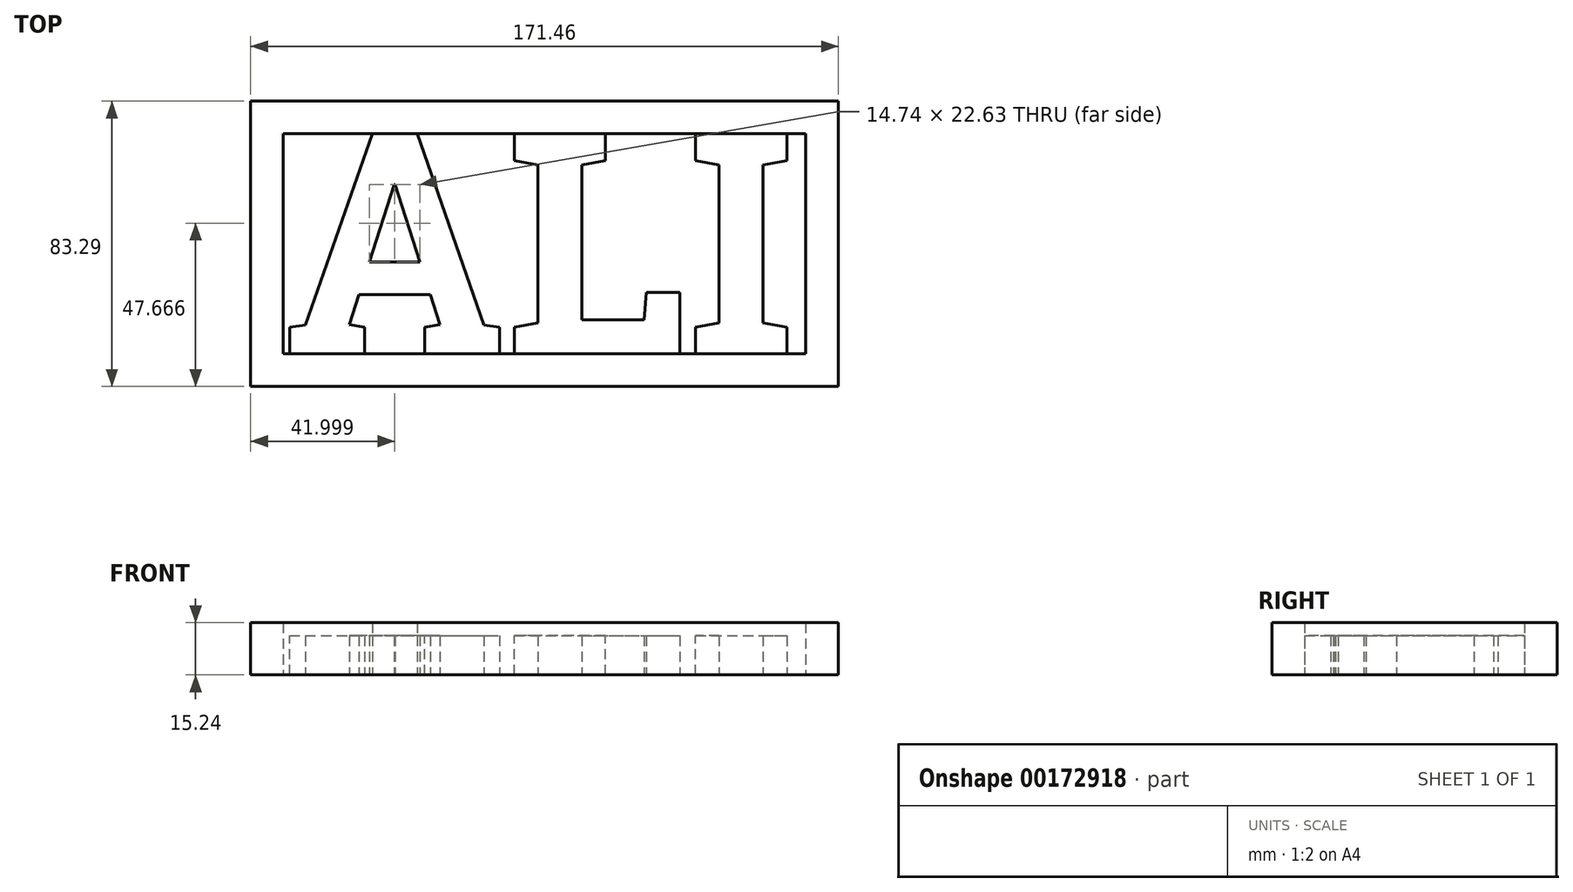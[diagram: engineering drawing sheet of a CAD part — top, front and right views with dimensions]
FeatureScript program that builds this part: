
annotation { "Feature Type Name" : "Feature", "Feature Type Description" : "" }
export const myFeature = defineFeature(function(context is Context, id is Id, definition is map)
    precondition{}
    {
        {
            var Q0;
            Q0=qCreatedBy(makeId("Top.planeOp"),FACE);
            var sketch = newSketch(context, id + "F0", { "sketchPlane" : qUnion([Q0])});
            skLineSegment(sketch, "E0.bottom", {"start": v(0, 0) * mm, "end": v(152.4, 0) * mm});
            skLineSegment(sketch, "E0.top", {"start": v(0, 9.53) * mm, "end": v(152.4, 9.53) * mm});
            skLineSegment(sketch, "E0.left", {"start": v(0, 0) * mm, "end": v(0, 9.53) * mm});
            skLineSegment(sketch, "E0.right", {"start": v(152.4, 0) * mm, "end": v(152.4, 9.53) * mm});
            skText(sketch, "E1", { "text": "ALI", "fontName": "RobotoSlab-Bold.ttf"});
            const initialGuessF0  = {"E1": [0, 0.00953, 1, 0, 0.06505]};
            skSetInitialGuess(sketch, initialGuessF0);
            skSolve(sketch);
        }
        {
            var Q0;
            Q0=qSketchRegion(id+"F0",true);
            extrude(context, id + "F1", {"entities" : qUnion([Q0]), "depth" : 11.43 * mm});
        }
        {
            var Q0;
            Q0=makeQuery(id+"F1.opExtrude","CAP_FACE",FACE,{"disambiguationData":[OSD([sQuery(id+"F0.wireOp",EDGE,"E0.bottom"),sQuery(id+"F0.wireOp",EDGE,"E0.top"),sQuery(id+"F0.wireOp",EDGE,"E0.left"),sQuery(id+"F0.wireOp",EDGE,"E0.right"),sQuery(id+"F0.wireOp",EDGE,"E1.sketch_text.stroke-0"),sQuery(id+"F0.wireOp",EDGE,"E1.sketch_text.stroke-1"),sQuery(id+"F0.wireOp",EDGE,"E1.sketch_text.stroke-2"),sQuery(id+"F0.wireOp",EDGE,"E1.sketch_text.stroke-3"),sQuery(id+"F0.wireOp",EDGE,"E1.sketch_text.stroke-4"),sQuery(id+"F0.wireOp",EDGE,"E1.sketch_text.stroke-5"),sQuery(id+"F0.wireOp",EDGE,"E1.sketch_text.stroke-6"),sQuery(id+"F0.wireOp",EDGE,"E1.sketch_text.stroke-7"),sQuery(id+"F0.wireOp",EDGE,"E1.sketch_text.stroke-8"),sQuery(id+"F0.wireOp",EDGE,"E1.sketch_text.stroke-9"),sQuery(id+"F0.wireOp",EDGE,"E1.sketch_text.stroke-10"),sQuery(id+"F0.wireOp",EDGE,"E1.sketch_text.stroke-11"),sQuery(id+"F0.wireOp",EDGE,"E1.sketch_text.stroke-12"),sQuery(id+"F0.wireOp",EDGE,"E1.sketch_text.stroke-13"),sQuery(id+"F0.wireOp",EDGE,"E1.sketch_text.stroke-14"),sQuery(id+"F0.wireOp",EDGE,"E1.sketch_text.stroke-15"),sQuery(id+"F0.wireOp",EDGE,"E1.sketch_text.stroke-16"),sQuery(id+"F0.wireOp",EDGE,"E1.sketch_text.stroke-17"),sQuery(id+"F0.wireOp",EDGE,"E1.sketch_text.stroke-18"),sQuery(id+"F0.wireOp",EDGE,"E1.sketch_text.stroke-19"),sQuery(id+"F0.wireOp",EDGE,"E1.sketch_text.stroke-20"),sQuery(id+"F0.wireOp",EDGE,"E1.sketch_text.stroke-21"),sQuery(id+"F0.wireOp",EDGE,"E1.sketch_text.stroke-22"),sQuery(id+"F0.wireOp",EDGE,"E1.sketch_text.stroke-23"),sQuery(id+"F0.wireOp",EDGE,"E1.sketch_text.stroke-24"),sQuery(id+"F0.wireOp",EDGE,"E1.sketch_text.stroke-25"),sQuery(id+"F0.wireOp",EDGE,"E1.sketch_text.stroke-26"),sQuery(id+"F0.wireOp",EDGE,"E1.sketch_text.stroke-27"),sQuery(id+"F0.wireOp",EDGE,"E1.sketch_text.stroke-28"),sQuery(id+"F0.wireOp",EDGE,"E1.sketch_text.stroke-29"),sQuery(id+"F0.wireOp",EDGE,"E1.sketch_text.stroke-30"),sQuery(id+"F0.wireOp",EDGE,"E1.sketch_text.stroke-31"),sQuery(id+"F0.wireOp",EDGE,"E1.sketch_text.stroke-32"),sQuery(id+"F0.wireOp",EDGE,"E1.sketch_text.stroke-33"),sQuery(id+"F0.wireOp",EDGE,"E1.sketch_text.stroke-34"),sQuery(id+"F0.wireOp",EDGE,"E1.sketch_text.stroke-35"),sQuery(id+"F0.wireOp",EDGE,"E1.sketch_text.stroke-36"),sQuery(id+"F0.wireOp",EDGE,"E1.sketch_text.stroke-37"),sQuery(id+"F0.wireOp",EDGE,"E1.sketch_text.stroke-38"),sQuery(id+"F0.wireOp",EDGE,"E1.sketch_text.stroke-39"),sQuery(id+"F0.wireOp",EDGE,"E1.sketch_text.stroke-40"),sQuery(id+"F0.wireOp",EDGE,"E1.sketch_text.stroke-42"),sQuery(id+"F0.wireOp",EDGE,"E1.sketch_text.stroke-43"),sQuery(id+"F0.wireOp",EDGE,"E1.sketch_text.stroke-44"),sQuery(id+"F0.wireOp",EDGE,"E1.sketch_text.stroke-45"),sQuery(id+"F0.wireOp",EDGE,"E1.sketch_text.stroke-46"),sQuery(id+"F0.wireOp",EDGE,"E1.sketch_text.stroke-47"),sQuery(id+"F0.wireOp",EDGE,"E1.sketch_text.stroke-48"),sQuery(id+"F0.wireOp",EDGE,"E1.sketch_text.stroke-50"),sQuery(id+"F0.wireOp",EDGE,"E1.sketch_text.stroke-51"),sQuery(id+"F0.wireOp",EDGE,"E1.sketch_text.stroke-52"),sQuery(id+"F0.wireOp",EDGE,"E1.sketch_text.stroke-53"),sQuery(id+"F0.wireOp",EDGE,"E1.sketch_text.stroke-54"),sQuery(id+"F0.wireOp",EDGE,"E1.sketch_text.stroke-55"),sQuery(id+"F0.wireOp",EDGE,"E1.sketch_text.stroke-56"),sQuery(id+"F0.wireOp",EDGE,"E1.sketch_text.stroke-57"),sQuery(id+"F0.wireOp",EDGE,"E1.sketch_text.stroke-58"),sQuery(id+"F0.wireOp",EDGE,"E1.sketch_text.stroke-59"),sQuery(id+"F0.wireOp",EDGE,"E1.sketch_text.stroke-60"),sQuery(id+"F0.wireOp",EDGE,"E1.sketch_text.stroke-62"),sQuery(id+"F0.wireOp",EDGE,"E1.sketch_text.stroke-63"),sQuery(id+"F0.wireOp",EDGE,"E1.sketch_text.stroke-64"),sQuery(id+"F0.wireOp",EDGE,"E1.sketch_text.stroke-65"),sQuery(id+"F0.wireOp",EDGE,"E1.sketch_text.stroke-66"),sQuery(id+"F0.wireOp",EDGE,"E1.sketch_text.stroke-67"),sQuery(id+"F0.wireOp",EDGE,"E1.sketch_text.stroke-68"),sQuery(id+"F0.wireOp",EDGE,"E1.sketch_text.stroke-69"),sQuery(id+"F0.wireOp",EDGE,"E1.sketch_text.stroke-70"),sQuery(id+"F0.wireOp",EDGE,"E1.sketch_text.stroke-71"),sQuery(id+"F0.wireOp",EDGE,"E1.sketch_text.stroke-72"),sQuery(id+"F0.wireOp",EDGE,"E1.sketch_text.stroke-73"),sQuery(id+"F0.wireOp",EDGE,"E1.sketch_text.stroke-75"),sQuery(id+"F0.wireOp",EDGE,"E1.sketch_text.stroke-76"),sQuery(id+"F0.wireOp",EDGE,"E1.sketch_text.stroke-77"),sQuery(id+"F0.wireOp",EDGE,"E1.sketch_text.stroke-78"),sQuery(id+"F0.wireOp",EDGE,"E1.sketch_text.stroke-79"),sQuery(id+"F0.wireOp",EDGE,"E1.sketch_text.stroke-80"),sQuery(id+"F0.wireOp",EDGE,"E1.sketch_text.stroke-81"),sQuery(id+"F0.wireOp",EDGE,"E1.sketch_text.stroke-82"),sQuery(id+"F0.wireOp",EDGE,"E1.sketch_text.stroke-83"),sQuery(id+"F0.wireOp",EDGE,"E1.sketch_text.stroke-84"),sQuery(id+"F0.wireOp",EDGE,"E1.sketch_text.stroke-85"),sQuery(id+"F0.wireOp",EDGE,"E1.sketch_text.stroke-86"),sQuery(id+"F0.wireOp",EDGE,"E1.sketch_text.stroke-87"),sQuery(id+"F0.wireOp",EDGE,"E1.sketch_text.stroke-88")])],"isStart":false});
            var sketch = newSketch(context, id + "F2", { "sketchPlane" : qUnion([Q0])});
            skLineSegment(sketch, "E2.bottom", {"start": v(0, 0) * mm, "end": v(152.4, 0) * mm});
            skLineSegment(sketch, "E2.top", {"start": v(0, 9.53) * mm, "end": v(152.4, 9.53) * mm});
            skLineSegment(sketch, "E2.left", {"start": v(0, 0) * mm, "end": v(0, 9.53) * mm});
            skLineSegment(sketch, "E2.right", {"start": v(152.4, 0) * mm, "end": v(152.4, 9.53) * mm});
            skSolve(sketch);
        }
        {
            var Q0;
            Q0=qSketchRegion(id+"F2",true);
            extrude(context, id + "F3", {"entities" : qUnion([Q0]), "operationType" : NewBodyOperationType.ADD, "depth" : 3.8 * mm});
        }
        {
            var Q0;
            Q0=makeQuery(id+"F1.opExtrude","CAP_FACE",FACE,{"disambiguationData":[OSD([sQuery(id+"F0.wireOp",EDGE,"E0.bottom"),sQuery(id+"F0.wireOp",EDGE,"E0.top"),sQuery(id+"F0.wireOp",EDGE,"E0.left"),sQuery(id+"F0.wireOp",EDGE,"E0.right"),sQuery(id+"F0.wireOp",EDGE,"E1.sketch_text.stroke-0"),sQuery(id+"F0.wireOp",EDGE,"E1.sketch_text.stroke-1"),sQuery(id+"F0.wireOp",EDGE,"E1.sketch_text.stroke-2"),sQuery(id+"F0.wireOp",EDGE,"E1.sketch_text.stroke-3"),sQuery(id+"F0.wireOp",EDGE,"E1.sketch_text.stroke-4"),sQuery(id+"F0.wireOp",EDGE,"E1.sketch_text.stroke-5"),sQuery(id+"F0.wireOp",EDGE,"E1.sketch_text.stroke-7"),sQuery(id+"F0.wireOp",EDGE,"E1.sketch_text.stroke-8"),sQuery(id+"F0.wireOp",EDGE,"E1.sketch_text.stroke-9"),sQuery(id+"F0.wireOp",EDGE,"E1.sketch_text.stroke-10"),sQuery(id+"F0.wireOp",EDGE,"E1.sketch_text.stroke-11"),sQuery(id+"F0.wireOp",EDGE,"E1.sketch_text.stroke-12"),sQuery(id+"F0.wireOp",EDGE,"E1.sketch_text.stroke-13"),sQuery(id+"F0.wireOp",EDGE,"E1.sketch_text.stroke-15"),sQuery(id+"F0.wireOp",EDGE,"E1.sketch_text.stroke-16"),sQuery(id+"F0.wireOp",EDGE,"E1.sketch_text.stroke-17"),sQuery(id+"F0.wireOp",EDGE,"E1.sketch_text.stroke-18"),sQuery(id+"F0.wireOp",EDGE,"E1.sketch_text.stroke-19"),sQuery(id+"F0.wireOp",EDGE,"E1.sketch_text.stroke-20"),sQuery(id+"F0.wireOp",EDGE,"E1.sketch_text.stroke-21"),sQuery(id+"F0.wireOp",EDGE,"E1.sketch_text.stroke-22"),sQuery(id+"F0.wireOp",EDGE,"E1.sketch_text.stroke-23"),sQuery(id+"F0.wireOp",EDGE,"E1.sketch_text.stroke-24"),sQuery(id+"F0.wireOp",EDGE,"E1.sketch_text.stroke-25"),sQuery(id+"F0.wireOp",EDGE,"E1.sketch_text.stroke-26"),sQuery(id+"F0.wireOp",EDGE,"E1.sketch_text.stroke-27"),sQuery(id+"F0.wireOp",EDGE,"E1.sketch_text.stroke-28"),sQuery(id+"F0.wireOp",EDGE,"E1.sketch_text.stroke-29"),sQuery(id+"F0.wireOp",EDGE,"E1.sketch_text.stroke-30"),sQuery(id+"F0.wireOp",EDGE,"E1.sketch_text.stroke-32"),sQuery(id+"F0.wireOp",EDGE,"E1.sketch_text.stroke-33"),sQuery(id+"F0.wireOp",EDGE,"E1.sketch_text.stroke-34"),sQuery(id+"F0.wireOp",EDGE,"E1.sketch_text.stroke-35"),sQuery(id+"F0.wireOp",EDGE,"E1.sketch_text.stroke-36"),sQuery(id+"F0.wireOp",EDGE,"E1.sketch_text.stroke-37"),sQuery(id+"F0.wireOp",EDGE,"E1.sketch_text.stroke-38"),sQuery(id+"F0.wireOp",EDGE,"E1.sketch_text.stroke-39"),sQuery(id+"F0.wireOp",EDGE,"E1.sketch_text.stroke-40"),sQuery(id+"F0.wireOp",EDGE,"E1.sketch_text.stroke-42"),sQuery(id+"F0.wireOp",EDGE,"E1.sketch_text.stroke-43"),sQuery(id+"F0.wireOp",EDGE,"E1.sketch_text.stroke-44"),sQuery(id+"F0.wireOp",EDGE,"E1.sketch_text.stroke-45"),sQuery(id+"F0.wireOp",EDGE,"E1.sketch_text.stroke-46"),sQuery(id+"F0.wireOp",EDGE,"E1.sketch_text.stroke-47"),sQuery(id+"F0.wireOp",EDGE,"E1.sketch_text.stroke-48"),sQuery(id+"F0.wireOp",EDGE,"E1.sketch_text.stroke-49"),sQuery(id+"F0.wireOp",EDGE,"E1.sketch_text.stroke-50"),sQuery(id+"F0.wireOp",EDGE,"E1.sketch_text.stroke-51"),sQuery(id+"F0.wireOp",EDGE,"E1.sketch_text.stroke-52"),sQuery(id+"F0.wireOp",EDGE,"E1.sketch_text.stroke-53"),sQuery(id+"F0.wireOp",EDGE,"E1.sketch_text.stroke-54"),sQuery(id+"F0.wireOp",EDGE,"E1.sketch_text.stroke-55"),sQuery(id+"F0.wireOp",EDGE,"E1.sketch_text.stroke-56"),sQuery(id+"F0.wireOp",EDGE,"E1.sketch_text.stroke-57"),sQuery(id+"F0.wireOp",EDGE,"E1.sketch_text.stroke-58"),sQuery(id+"F0.wireOp",EDGE,"E1.sketch_text.stroke-59"),sQuery(id+"F0.wireOp",EDGE,"E1.sketch_text.stroke-60"),sQuery(id+"F0.wireOp",EDGE,"E1.sketch_text.stroke-61"),sQuery(id+"F0.wireOp",EDGE,"E1.sketch_text.stroke-62"),sQuery(id+"F0.wireOp",EDGE,"E1.sketch_text.stroke-64"),sQuery(id+"F0.wireOp",EDGE,"E1.sketch_text.stroke-65"),sQuery(id+"F0.wireOp",EDGE,"E1.sketch_text.stroke-66"),sQuery(id+"F0.wireOp",EDGE,"E1.sketch_text.stroke-67")])],"isStart":true});
            var sketch = newSketch(context, id + "F4", { "sketchPlane" : qUnion([Q0])});
            skLineSegment(sketch, "E3.bottom", {"start": v(0, -73.76) * mm, "end": v(152.4, -73.76) * mm});
            skLineSegment(sketch, "E3.top", {"start": v(0, -83.29) * mm, "end": v(152.4, -83.29) * mm});
            skLineSegment(sketch, "E3.left", {"start": v(0, -73.76) * mm, "end": v(0, -83.29) * mm});
            skLineSegment(sketch, "E3.right", {"start": v(152.4, -73.76) * mm, "end": v(152.4, -83.29) * mm});
            skLineSegment(sketch, "E4.bottom", {"start": v(0, -83.29) * mm, "end": v(-9.52, -83.29) * mm});
            skLineSegment(sketch, "E4.top", {"start": v(0, 0) * mm, "end": v(-9.53, 0) * mm});
            skLineSegment(sketch, "E4.left", {"start": v(0, -83.29) * mm, "end": v(0, 0) * mm});
            skLineSegment(sketch, "E4.right", {"start": v(-9.52, -83.29) * mm, "end": v(-9.53, 0) * mm});
            skLineSegment(sketch, "E5.bottom", {"start": v(152.4, -83.29) * mm, "end": v(161.93, -83.29) * mm});
            skLineSegment(sketch, "E5.top", {"start": v(152.4, 0) * mm, "end": v(161.93, 0) * mm});
            skLineSegment(sketch, "E5.left", {"start": v(152.4, -83.29) * mm, "end": v(152.4, 0) * mm});
            skLineSegment(sketch, "E5.right", {"start": v(161.93, -83.29) * mm, "end": v(161.93, 0) * mm});
            skSolve(sketch);
        }
        {
            var Q0;
            Q0=makeQuery(id+"F4.imprint","IMPRINT",FACE,{"disambiguationData":[TD([[makeQuery(id+"F4.imprint","IMPRINT",EDGE,{"derivedFrom":sQuery(id+"F4.wireOp",EDGE,"E3.top")}),1.0]])]});
            var Q1;
            {var subQ5=sQuery(id+"F4.wireOp",EDGE,"E4.bottom");Q1=makeQuery(id+"F4.imprint","IMPRINT",FACE,{"disambiguationData":[TD([[makeQuery(id+"F4.imprint","IMPRINT",EDGE,{"derivedFrom":subQ5}),-1.0]])]});}
            var Q2;
            {var subQ4=sQuery(id+"F4.wireOp",EDGE,"E5.bottom");Q2=makeQuery(id+"F4.imprint","IMPRINT",FACE,{"disambiguationData":[TD([[makeQuery(id+"F4.imprint","IMPRINT",EDGE,{"derivedFrom":subQ4}),1.0]])]});}
            var Q3;
            Q3=makeQuery(id+"F3.opExtrude","CAP_FACE",FACE,{"disambiguationData":[OSD([sQuery(id+"F2.wireOp",EDGE,"E2.bottom"),sQuery(id+"F2.wireOp",EDGE,"E2.top"),sQuery(id+"F2.wireOp",EDGE,"E2.left"),sQuery(id+"F2.wireOp",EDGE,"E2.right")])],"isStart":false});
            extrude(context, id + "F5", {"entities" : qUnion([Q0, Q1, Q2]), "operationType" : NewBodyOperationType.ADD, "endBound" : BoundingType.UP_TO_SURFACE, "oppositeDirection" : true, "endBoundEntityFace" : qUnion([Q3]), "depth" : 25.4 * mm});
        }
    });
